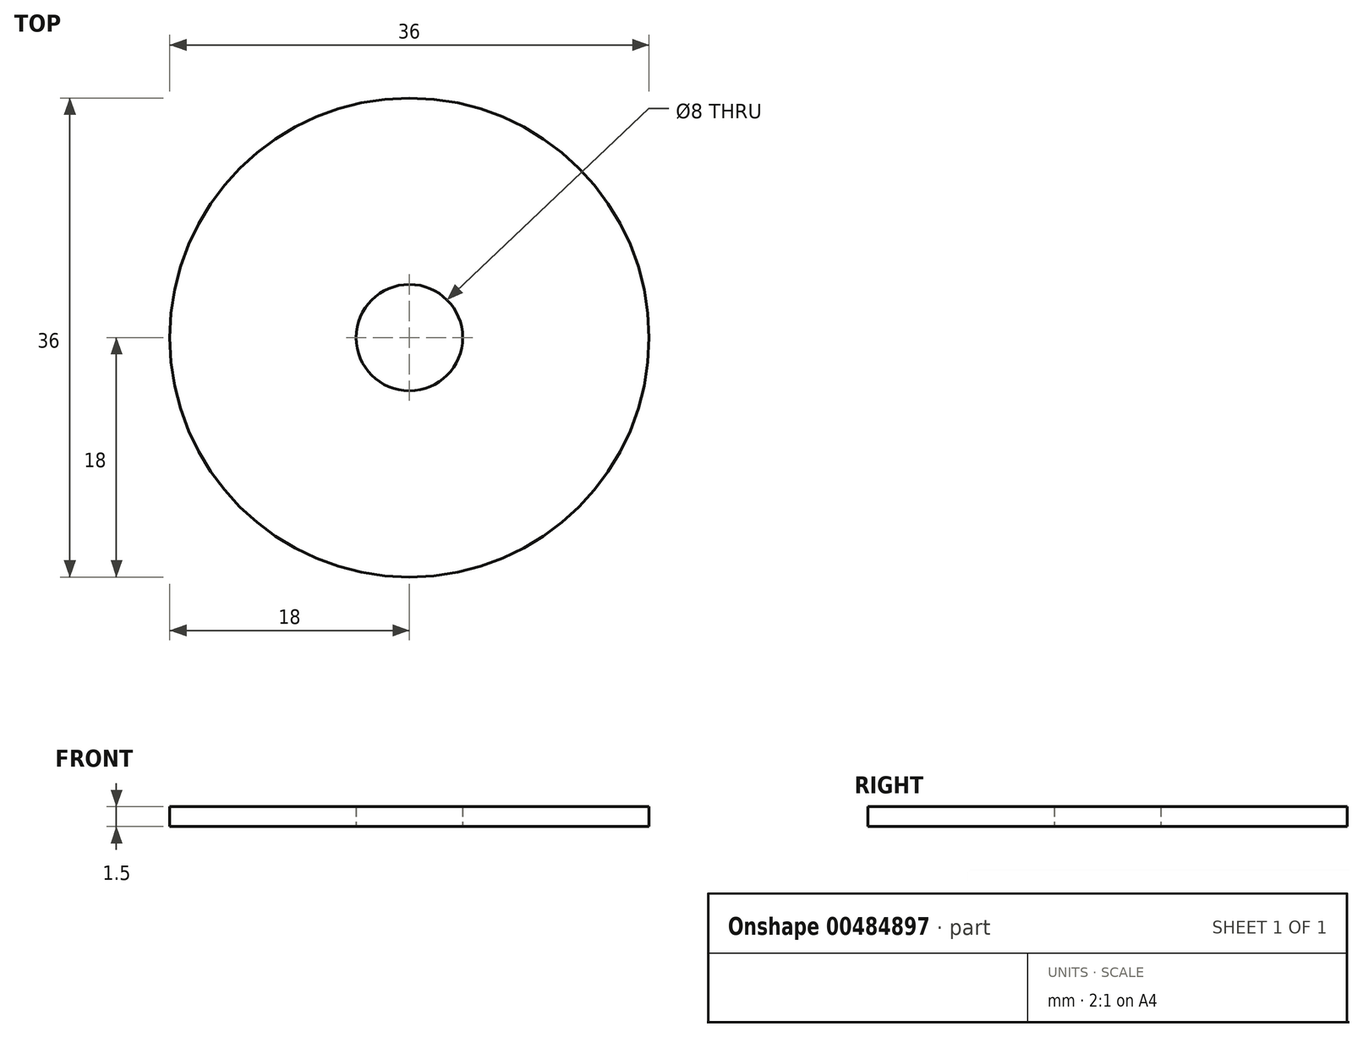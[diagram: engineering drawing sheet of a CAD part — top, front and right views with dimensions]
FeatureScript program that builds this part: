
annotation { "Feature Type Name" : "Feature", "Feature Type Description" : "" }
export const myFeature = defineFeature(function(context is Context, id is Id, definition is map)
    precondition{}
    {
        {
            var Q0;
            Q0=qCreatedBy(makeId("Top.planeOp"),FACE);
            var sketch = newSketch(context, id + "F0", { "sketchPlane" : qUnion([Q0])});
            skCircle(sketch, "E0", {"center": v(0, 0) * mm, "radius": 18 * mm});
            skCircle(sketch, "E1", {"center": v(0, 0) * mm, "radius": 4 * mm});
            skSolve(sketch);
        }
        {
            var Q0;
            Q0=makeQuery(id+"F0.imprint","IMPRINT",FACE,{"disambiguationData":[TD([[makeQuery(id+"F0.imprint","IMPRINT",EDGE,{"derivedFrom":sQuery(id+"F0.wireOp",EDGE,"E0")}),1.0]])]});
            extrude(context, id + "F1", {"entities" : qUnion([Q0]), "depth" : 1.5 * mm, "offsetDistance" : 25 * mm});
        }
    });
